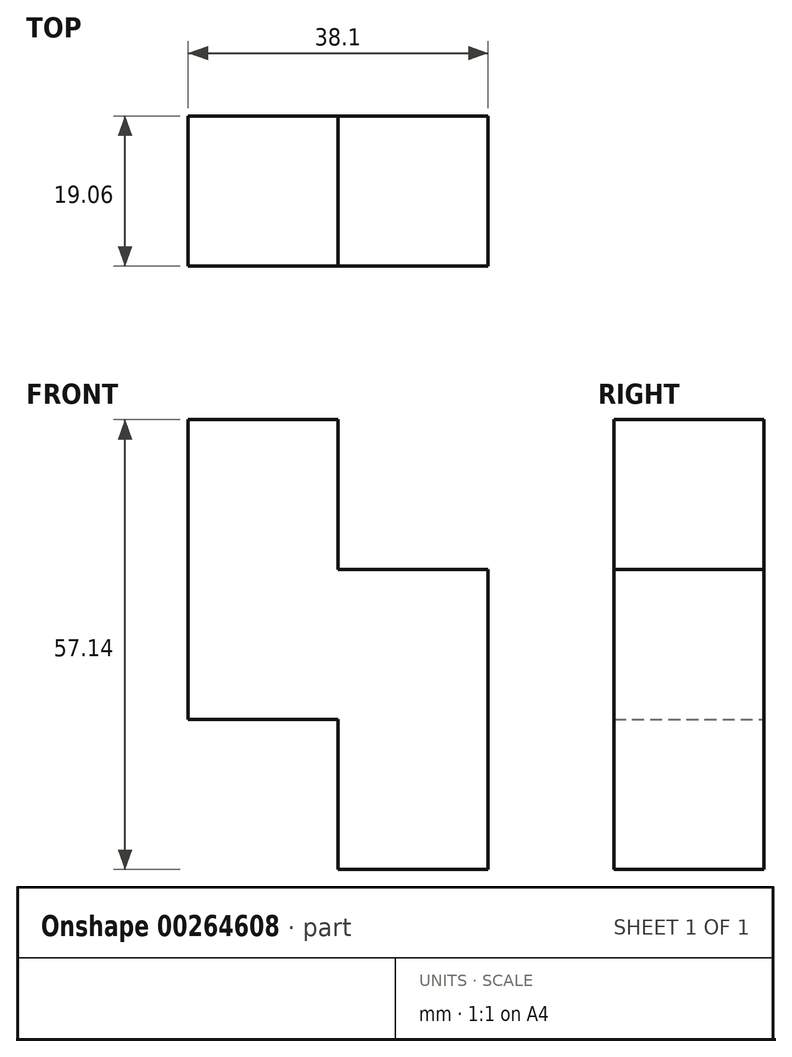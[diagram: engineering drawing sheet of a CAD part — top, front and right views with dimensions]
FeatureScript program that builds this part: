
annotation { "Feature Type Name" : "Feature", "Feature Type Description" : "" }
export const myFeature = defineFeature(function(context is Context, id is Id, definition is map)
    precondition{}
    {
        {
            var Q0;
            Q0=qCreatedBy(makeId("Front.planeOp"),FACE);
            var sketch = newSketch(context, id + "F0", { "sketchPlane" : qUnion([Q0])});
            skLineSegment(sketch, "E0.bottom", {"start": v(9.53, 9.53) * mm, "end": v(-9.53, 9.53) * mm});
            skLineSegment(sketch, "E0.top", {"start": v(9.53, -9.52) * mm, "end": v(-9.53, -9.52) * mm});
            skLineSegment(sketch, "E0.left", {"start": v(9.53, 9.53) * mm, "end": v(9.53, -9.52) * mm});
            skLineSegment(sketch, "E0.right", {"start": v(-9.53, 9.53) * mm, "end": v(-9.53, -9.52) * mm});
            skPoint(sketch, "E0.middle", {"position": v(0, 0) * mm});
            skLineSegment(sketch, "E1.bottom", {"start": v(9.53, 28.57) * mm, "end": v(-9.52, 28.57) * mm});
            skLineSegment(sketch, "E1.top", {"start": v(9.53, 9.53) * mm, "end": v(-9.52, 9.53) * mm});
            skLineSegment(sketch, "E1.left", {"start": v(9.53, 28.57) * mm, "end": v(9.53, 9.52) * mm});
            skLineSegment(sketch, "E1.right", {"start": v(-9.52, 28.58) * mm, "end": v(-9.52, 9.53) * mm});
            skPoint(sketch, "E1.middle", {"position": v(0, 19.05) * mm});
            skLineSegment(sketch, "E2.top", {"start": v(28.58, -9.52) * mm, "end": v(9.53, -9.52) * mm});
            skLineSegment(sketch, "E2.left", {"start": v(28.58, 9.52) * mm, "end": v(28.58, -9.52) * mm});
            skLineSegment(sketch, "E3.top", {"start": v(28.58, 9.53) * mm, "end": v(9.53, 9.53) * mm});
            skLineSegment(sketch, "E4.top", {"start": v(9.53, -9.53) * mm, "end": v(28.58, -9.53) * mm});
            skLineSegment(sketch, "E4.left", {"start": v(9.53, -28.57) * mm, "end": v(9.53, -9.53) * mm});
            skLineSegment(sketch, "E4.right", {"start": v(28.58, -28.57) * mm, "end": v(28.58, -9.52) * mm});
            skLineSegment(sketch, "E5.top", {"start": v(9.52, -28.57) * mm, "end": v(28.58, -28.57) * mm});
            skSolve(sketch);
        }
        {
            var Q0;
            Q0 = qSketchRegion(id + "F0", true);
            extrude(context, id + "F1", {"entities" : qUnion([Q0]), "endBound" : BoundingType.SYMMETRIC, "depth" : 19.05 * mm});
        }
    });
